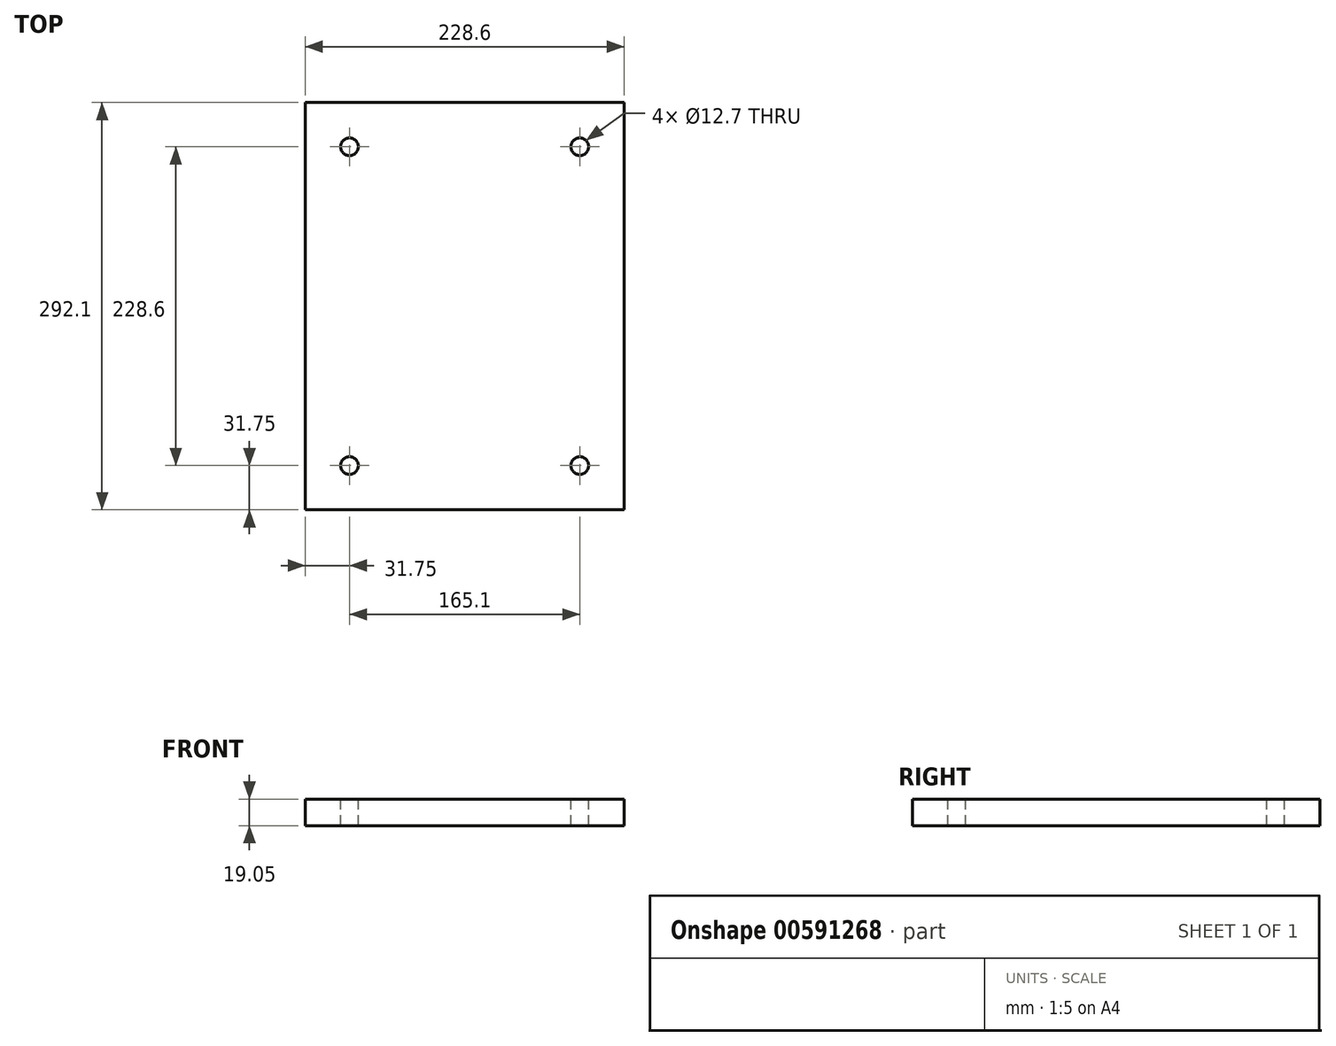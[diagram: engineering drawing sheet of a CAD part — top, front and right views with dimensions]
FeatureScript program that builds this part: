
annotation { "Feature Type Name" : "Feature", "Feature Type Description" : "" }
export const myFeature = defineFeature(function(context is Context, id is Id, definition is map)
    precondition{}
    {
        {
            var Q0;
            Q0=qCreatedBy(makeId("Top.planeOp"),FACE);
            var sketch = newSketch(context, id + "F0", { "sketchPlane" : qUnion([Q0])});
            skLineSegment(sketch, "E0.bottom", {"start": v(114.3, -146.05) * mm, "end": v(-114.3, -146.05) * mm});
            skLineSegment(sketch, "E0.top", {"start": v(114.3, 146.05) * mm, "end": v(-114.3, 146.05) * mm});
            skLineSegment(sketch, "E0.left", {"start": v(114.3, -146.05) * mm, "end": v(114.3, 146.05) * mm});
            skLineSegment(sketch, "E0.right", {"start": v(-114.3, -146.05) * mm, "end": v(-114.3, 146.05) * mm});
            skPoint(sketch, "E0.middle", {"position": v(0, 0) * mm});
            skSolve(sketch);
        }
        {
            var Q0;
            Q0 = qSketchRegion(id + "F0", true);
            extrude(context, id + "F1", {"entities" : qUnion([Q0]), "depth" : 19.05 * mm, "offsetDistance" : 25.4 * mm});
        }
        {
            var Q0;
            Q0=makeQuery(id+"F1.opExtrude","CAP_FACE",FACE,{"disambiguationData":[OSD([sQuery(id+"F0.wireOp",EDGE,"E0.bottom"),sQuery(id+"F0.wireOp",EDGE,"E0.top"),sQuery(id+"F0.wireOp",EDGE,"E0.left"),sQuery(id+"F0.wireOp",EDGE,"E0.right")])],"isStart":false});
            var sketch = newSketch(context, id + "F2", { "sketchPlane" : qUnion([Q0])});
            skCircle(sketch, "E1", {"center": v(-82.55, 114.3) * mm, "radius": 6.35 * mm});
            skCircle(sketch, "E2", {"center": v(82.55, 114.3) * mm, "radius": 6.35 * mm});
            skCircle(sketch, "E3", {"center": v(-82.55, -114.3) * mm, "radius": 6.35 * mm});
            skCircle(sketch, "E4", {"center": v(82.55, -114.3) * mm, "radius": 6.35 * mm});
            skSolve(sketch);
        }
        {
            var Q0;
            Q0=makeQuery(id+"F2.imprint","IMPRINT",FACE,{"disambiguationData":[TD([[makeQuery(id+"F2.imprint","IMPRINT",EDGE,{"derivedFrom":sQuery(id+"F2.wireOp",EDGE,"E1")}),1.0]])]});
            var Q1;
            Q1=makeQuery(id+"F2.imprint","IMPRINT",FACE,{"disambiguationData":[TD([[makeQuery(id+"F2.imprint","IMPRINT",EDGE,{"derivedFrom":sQuery(id+"F2.wireOp",EDGE,"E2")}),1.0]])]});
            var Q2;
            Q2=makeQuery(id+"F2.imprint","IMPRINT",FACE,{"disambiguationData":[TD([[makeQuery(id+"F2.imprint","IMPRINT",EDGE,{"derivedFrom":sQuery(id+"F2.wireOp",EDGE,"E4")}),1.0]])]});
            var Q3;
            Q3=makeQuery(id+"F2.imprint","IMPRINT",FACE,{"disambiguationData":[TD([[makeQuery(id+"F2.imprint","IMPRINT",EDGE,{"derivedFrom":sQuery(id+"F2.wireOp",EDGE,"E3")}),1.0]])]});
            extrude(context, id + "F3", {"entities" : qUnion([Q0, Q1, Q2, Q3]), "operationType" : NewBodyOperationType.REMOVE, "oppositeDirection" : true, "depth" : 25.4 * mm, "offsetDistance" : 25.4 * mm});
        }
    });
